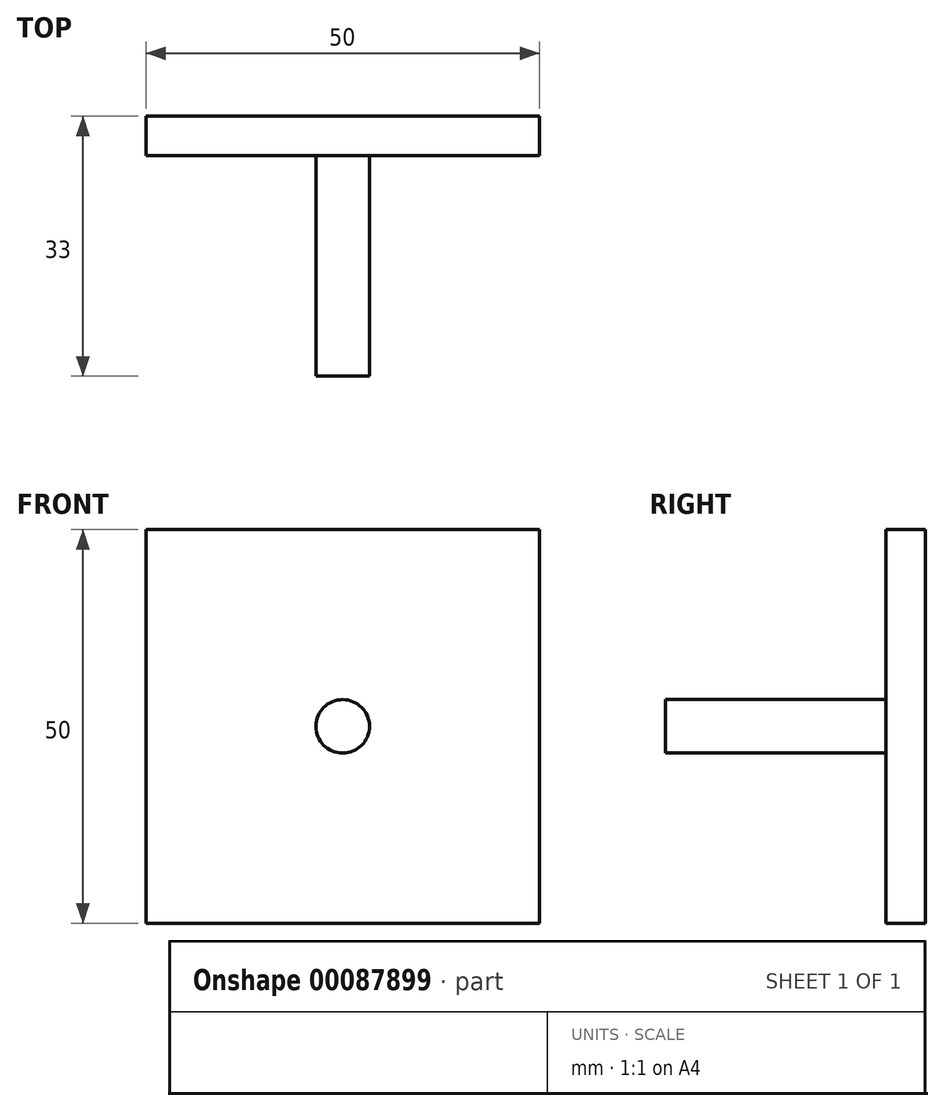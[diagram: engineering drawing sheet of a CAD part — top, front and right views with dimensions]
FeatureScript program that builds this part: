
annotation { "Feature Type Name" : "Feature", "Feature Type Description" : "" }
export const myFeature = defineFeature(function(context is Context, id is Id, definition is map)
    precondition{}
    {
        {
            var Q0;
            Q0=qCreatedBy(makeId("Front.planeOp"),FACE);
            var sketch = newSketch(context, id + "F0", { "sketchPlane" : qUnion([Q0])});
            skCircle(sketch, "E0", {"center": v(0, 0) * mm, "radius": 3.4 * mm});
            skLineSegment(sketch, "E1.bottom", {"start": v(25, 25) * mm, "end": v(-25, 25) * mm});
            skLineSegment(sketch, "E1.top", {"start": v(25, -25) * mm, "end": v(-25, -25) * mm});
            skLineSegment(sketch, "E1.left", {"start": v(25, 25) * mm, "end": v(25, -25) * mm});
            skLineSegment(sketch, "E1.right", {"start": v(-25, 25) * mm, "end": v(-25, -25) * mm});
            skSolve(sketch);
        }
        {
            var Q0;
            Q0=makeQuery(id+"F0.imprint","IMPRINT",FACE,{"disambiguationData":[TD([[makeQuery(id+"F0.imprint","IMPRINT",EDGE,{"derivedFrom":sQuery(id+"F0.wireOp",EDGE,"E0")}),-1.0]])]});
            extrude(context, id + "F1", {"entities" : qUnion([Q0]), "depth" : 5 * mm});
        }
        {
            var Q0;
            Q0=makeQuery(id+"F0.imprint","IMPRINT",FACE,{"disambiguationData":[TD([[makeQuery(id+"F0.imprint","IMPRINT",EDGE,{"derivedFrom":sQuery(id+"F0.wireOp",EDGE,"E0")}),1.0]])]});
            extrude(context, id + "F2", {"entities" : qUnion([Q0]), "operationType" : NewBodyOperationType.ADD, "depth" : 33 * mm});
        }
    });
